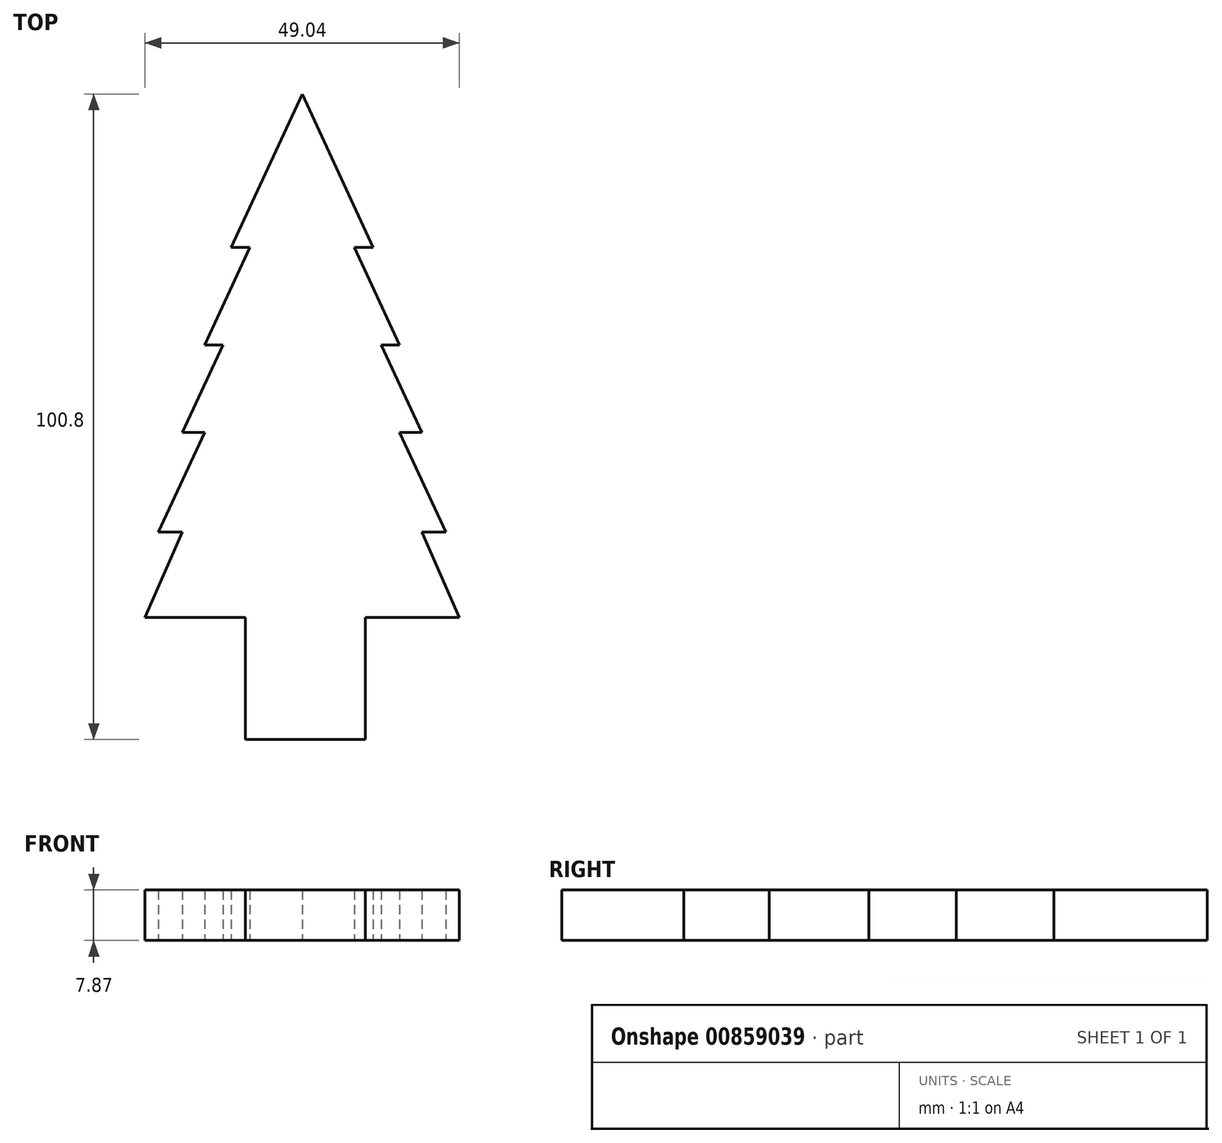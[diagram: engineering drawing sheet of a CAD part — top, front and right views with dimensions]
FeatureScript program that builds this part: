
annotation { "Feature Type Name" : "Feature", "Feature Type Description" : "" }
export const myFeature = defineFeature(function(context is Context, id is Id, definition is map)
    precondition{}
    {
        {
            var Q0;
            Q0=qCreatedBy(makeId("Top.planeOp"),FACE);
            var sketch = newSketch(context, id + "F0", { "sketchPlane" : qUnion([Q0])});
            skLineSegment(sketch, "E0", {"start": v(0, 52.82) * mm, "end": v(-11.08, 28.87) * mm});
            skLineSegment(sketch, "E1", {"start": v(-11.08, 28.87) * mm, "end": v(-8.19, 28.87) * mm});
            skLineSegment(sketch, "E2", {"start": v(-8.19, 28.87) * mm, "end": v(-15.22, 13.66) * mm});
            skLineSegment(sketch, "E3", {"start": v(-15.22, 13.66) * mm, "end": v(-12.36, 13.66) * mm});
            skLineSegment(sketch, "E4", {"start": v(-12.36, 13.66) * mm, "end": v(-18.68, 0) * mm});
            skLineSegment(sketch, "E5", {"start": v(-18.68, 0) * mm, "end": v(-15.22, 0) * mm});
            skLineSegment(sketch, "E6", {"start": v(-15.22, 0) * mm, "end": v(-22.43, -15.57) * mm});
            skLineSegment(sketch, "E7", {"start": v(-22.43, -15.57) * mm, "end": v(-18.68, -15.57) * mm});
            skLineSegment(sketch, "E8", {"start": v(-18.68, -15.57) * mm, "end": v(-24.52, -28.88) * mm});
            skLineSegment(sketch, "E9", {"start": v(0, 52.82) * mm, "end": v(0, -47.98) * mm, "construction": true});
            skLineSegment(sketch, "E10", {"start": v(-24.52, -28.88) * mm, "end": v(-8.84, -28.88) * mm});
            skLineSegment(sketch, "E11", {"start": v(-8.84, -28.88) * mm, "end": v(-8.84, -47.98) * mm});
            skLineSegment(sketch, "E12", {"start": v(-8.84, -47.98) * mm, "end": v(0, -47.98) * mm});
            skLineSegment(sketch, "E13.MirrorCS", {"start": v(0, 52.82) * mm, "end": v(11.08, 28.87) * mm});
            skLineSegment(sketch, "E14.MirrorCS", {"start": v(8.19, 28.87) * mm, "end": v(15.22, 13.66) * mm});
            skLineSegment(sketch, "E15.MirrorCS", {"start": v(12.36, 13.66) * mm, "end": v(18.68, 0) * mm});
            skLineSegment(sketch, "E16.MirrorCS", {"start": v(15.22, 0) * mm, "end": v(22.43, -15.57) * mm});
            skLineSegment(sketch, "E17.MirrorCS", {"start": v(18.68, -15.57) * mm, "end": v(24.52, -28.88) * mm});
            skLineSegment(sketch, "E18.MirrorCS", {"start": v(22.43, -15.57) * mm, "end": v(18.68, -15.57) * mm});
            skLineSegment(sketch, "E19.MirrorCS", {"start": v(18.68, 0) * mm, "end": v(15.22, 0) * mm});
            skLineSegment(sketch, "E20", {"start": v(24.52, -28.88) * mm, "end": v(9.84, -28.88) * mm});
            skLineSegment(sketch, "E21", {"start": v(0, -47.98) * mm, "end": v(9.84, -47.98) * mm});
            skLineSegment(sketch, "E22", {"start": v(9.84, -47.98) * mm, "end": v(9.84, -28.88) * mm});
            skLineSegment(sketch, "E23", {"start": v(15.22, 13.66) * mm, "end": v(12.36, 13.66) * mm});
            skLineSegment(sketch, "E24", {"start": v(11.08, 28.87) * mm, "end": v(8.19, 28.87) * mm});
            skSolve(sketch);
        }
        {
            var Q0;
            Q0=makeQuery(id+"F0.imprint","IMPRINT",FACE,{"disambiguationData":[TD([[makeQuery(id+"F0.imprint","IMPRINT",EDGE,{"derivedFrom":sQuery(id+"F0.wireOp",EDGE,"E0")}),1.0]])]});
            extrude(context, id + "F1", {"entities" : qUnion([Q0]), "depth" : 7.87 * mm, "offsetDistance" : 25.4 * mm});
        }
    });
